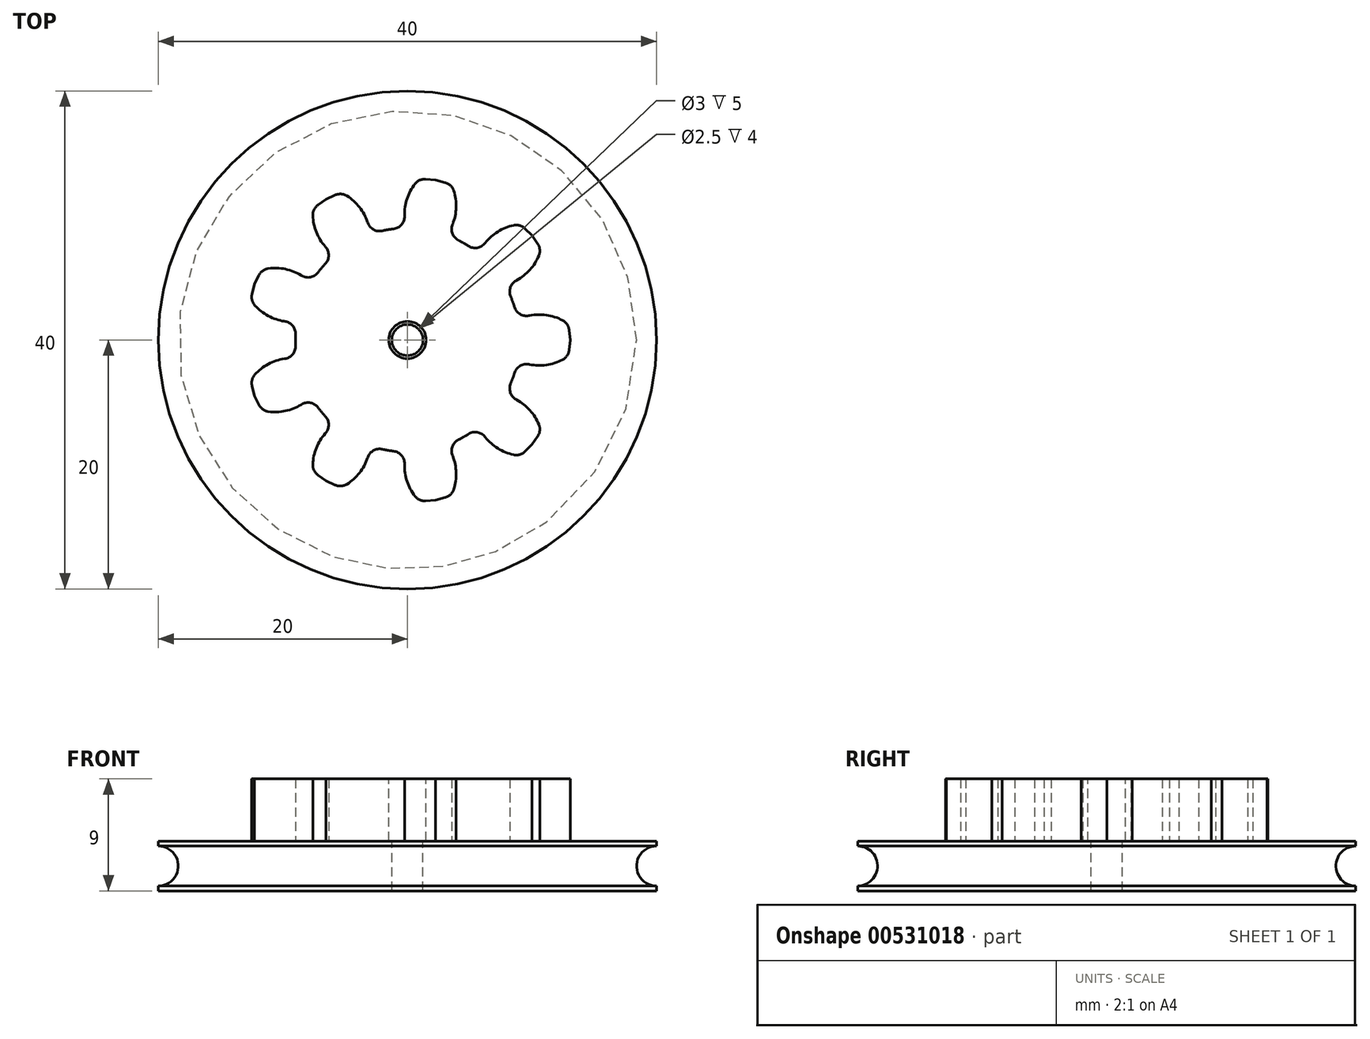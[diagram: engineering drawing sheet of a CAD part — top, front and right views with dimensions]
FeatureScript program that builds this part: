
annotation { "Feature Type Name" : "Feature", "Feature Type Description" : "" }
export const myFeature = defineFeature(function(context is Context, id is Id, definition is map)
    precondition{}
    {
        {
            var Q0;
            Q0=qCreatedBy(makeId("Top.planeOp"),FACE);
            var sketch = newSketch(context, id + "F0", { "sketchPlane" : qUnion([Q0])});
            skCircle(sketch, "E0", {"center": v(0, 0) * mm, "radius": 9 * mm, "construction": true});
            skLineSegment(sketch, "E1", {"start": v(0, 0) * mm, "end": v(11.56, 4.83) * mm, "construction": true});
            skLineSegment(sketch, "E2", {"start": v(0, 0) * mm, "end": v(13.01, 0) * mm, "construction": true});
            skLineSegment(sketch, "E3", {"start": v(0, 0) * mm, "end": v(8.3, 3.47) * mm});
            skLineSegment(sketch, "E4", {"start": v(0, 0) * mm, "end": v(9, 0) * mm});
            skLineSegment(sketch, "E5", {"start": v(0, 0) * mm, "end": v(9.8, 1.96) * mm, "construction": true});
            skLineSegment(sketch, "E6", {"start": v(0, 0) * mm, "end": v(12.94, 1.28) * mm, "construction": true});
            skArc(sketch, "E7", {"start": v(8.3, 3.47) * mm, "mid": v(8.46, 3.06) * mm, "end": v(8.6, 2.64) * mm});
            skLineSegment(sketch, "E8", {"start": v(9.76, 1.96) * mm, "end": v(9.8, 1.96) * mm});
            skLineSegment(sketch, "E9", {"start": v(12.98, 0.8) * mm, "end": v(13.06, 0) * mm});
            skLineSegment(sketch, "E10.MirrorCS", {"start": v(0, 0) * mm, "end": v(8.3, -3.47) * mm});
            skArc(sketch, "E11.MirrorCS", {"start": v(8.3, -3.47) * mm, "mid": v(8.46, -3.06) * mm, "end": v(8.6, -2.64) * mm});
            skLineSegment(sketch, "E12.MirrorCS", {"start": v(9.76, -1.96) * mm, "end": v(9.8, -1.96) * mm});
            skLineSegment(sketch, "E13.MirrorCS", {"start": v(12.98, -0.8) * mm, "end": v(13.06, 0) * mm});
            skPoint(sketch, "E14.visualSharp", {"position": v(8.82, 1.77) * mm});
            skArc(sketch, "E14.filletArc", {"start": v(8.6, 2.64) * mm, "mid": v(9.05, 2.08) * mm, "end": v(9.76, 1.96) * mm});
            skPoint(sketch, "E15.visualSharp", {"position": v(8.82, -1.77) * mm});
            skArc(sketch, "E15.filletArc", {"start": v(9.76, -1.96) * mm, "mid": v(9.05, -2.08) * mm, "end": v(8.6, -2.64) * mm});
            skPoint(sketch, "E16.visualSharp", {"position": v(12.94, -1.28) * mm});
            skArc(sketch, "E16.filletArc", {"start": v(12.46, -1.58) * mm, "mid": v(12.82, -1.26) * mm, "end": v(12.98, -0.8) * mm});
            skPoint(sketch, "E17.visualSharp", {"position": v(12.94, 1.28) * mm});
            skArc(sketch, "E17.filletArc", {"start": v(12.98, 0.8) * mm, "mid": v(12.82, 1.26) * mm, "end": v(12.46, 1.58) * mm});
            skArc(sketch, "E18", {"start": v(12.46, 1.58) * mm, "mid": v(11.16, 2) * mm, "end": v(9.8, 1.96) * mm});
            skArc(sketch, "E19", {"start": v(9.8, -1.96) * mm, "mid": v(11.16, -2) * mm, "end": v(12.46, -1.58) * mm});
            skSolve(sketch);
        }
        {
            var Q0;
            Q0=makeQuery(id+"F0.imprint","IMPRINT",FACE,{"disambiguationData":[TD([[makeQuery(id+"F0.imprint","IMPRINT",EDGE,{"derivedFrom":sQuery(id+"F0.wireOp",EDGE,"E3")}),-1.0]])]});
            extrude(context, id + "F1", {"entities" : qUnion([Q0]), "depth" : 5 * mm, "offsetDistance" : 25 * mm});
        }
        {
            var Q0;
            Q0=makeQuery(id+"F1.opExtrude","SWEPT_BODY",BODY,{"disambiguationData":[OSD([sQuery(id+"F0.wireOp",EDGE,"E3"),sQuery(id+"F0.wireOp",EDGE,"E7"),sQuery(id+"F0.wireOp",EDGE,"E8"),sQuery(id+"F0.wireOp",EDGE,"2mDmJFzi-9lNi-O13z-yd6C-LpkLtRZ1Arxh"),sQuery(id+"F0.wireOp",EDGE,"E9"),sQuery(id+"F0.wireOp",EDGE,"E10.MirrorCS"),sQuery(id+"F0.wireOp",EDGE,"E11.MirrorCS"),sQuery(id+"F0.wireOp",EDGE,"E12.MirrorCS"),sQuery(id+"F0.wireOp",EDGE,"b2a42f57-c3ba-47de-accf-343e7495cc910.MirrorCS"),sQuery(id+"F0.wireOp",EDGE,"E13.MirrorCS"),sQuery(id+"F0.wireOp",EDGE,"E14.filletArc"),sQuery(id+"F0.wireOp",EDGE,"E15.filletArc"),sQuery(id+"F0.wireOp",EDGE,"E16.filletArc"),sQuery(id+"F0.wireOp",EDGE,"E17.filletArc")])]});
            var Q1;
            Q1=makeQuery(id+"F1.opExtrude","SWEPT_EDGE",EDGE,{"disambiguationData":[OSD([sQuery(id+"F0.wireOp",EDGE,"E3"),sQuery(id+"F0.wireOp",EDGE,"E10.MirrorCS")])]});
            circularPattern(context, id + "F2", {"entities" : qUnion([Q0]), "axis" : qUnion([Q1]), "angle" : 360 * degree, "instanceCount" : 9, "equalSpace" : true, "computeTransformsWithoutBuiltin" : true});
        }
        {
            var Q0;
            Q0=makeQuery(id+"F2.opPattern","COPY",BODY,{"derivedFrom":makeQuery(id+"F1.opExtrude","SWEPT_BODY",BODY,{"disambiguationData":[OSD([sQuery(id+"F0.wireOp",EDGE,"E3"),sQuery(id+"F0.wireOp",EDGE,"E7"),sQuery(id+"F0.wireOp",EDGE,"E8"),sQuery(id+"F0.wireOp",EDGE,"2mDmJFzi-9lNi-O13z-yd6C-LpkLtRZ1Arxh"),sQuery(id+"F0.wireOp",EDGE,"E9"),sQuery(id+"F0.wireOp",EDGE,"E10.MirrorCS"),sQuery(id+"F0.wireOp",EDGE,"E11.MirrorCS"),sQuery(id+"F0.wireOp",EDGE,"E12.MirrorCS"),sQuery(id+"F0.wireOp",EDGE,"b2a42f57-c3ba-47de-accf-343e7495cc910.MirrorCS"),sQuery(id+"F0.wireOp",EDGE,"E13.MirrorCS"),sQuery(id+"F0.wireOp",EDGE,"E14.filletArc"),sQuery(id+"F0.wireOp",EDGE,"E15.filletArc"),sQuery(id+"F0.wireOp",EDGE,"E16.filletArc"),sQuery(id+"F0.wireOp",EDGE,"E17.filletArc")])]}),"instanceName":"7"});
            var Q1;
            Q1=makeQuery(id+"F2.opPattern","COPY",BODY,{"derivedFrom":makeQuery(id+"F1.opExtrude","SWEPT_BODY",BODY,{"disambiguationData":[OSD([sQuery(id+"F0.wireOp",EDGE,"E3"),sQuery(id+"F0.wireOp",EDGE,"E7"),sQuery(id+"F0.wireOp",EDGE,"E8"),sQuery(id+"F0.wireOp",EDGE,"2mDmJFzi-9lNi-O13z-yd6C-LpkLtRZ1Arxh"),sQuery(id+"F0.wireOp",EDGE,"E9"),sQuery(id+"F0.wireOp",EDGE,"E10.MirrorCS"),sQuery(id+"F0.wireOp",EDGE,"E11.MirrorCS"),sQuery(id+"F0.wireOp",EDGE,"E12.MirrorCS"),sQuery(id+"F0.wireOp",EDGE,"b2a42f57-c3ba-47de-accf-343e7495cc910.MirrorCS"),sQuery(id+"F0.wireOp",EDGE,"E13.MirrorCS"),sQuery(id+"F0.wireOp",EDGE,"E14.filletArc"),sQuery(id+"F0.wireOp",EDGE,"E15.filletArc"),sQuery(id+"F0.wireOp",EDGE,"E16.filletArc"),sQuery(id+"F0.wireOp",EDGE,"E17.filletArc")])]}),"instanceName":"6"});
            var Q2;
            Q2=makeQuery(id+"F2.opPattern","COPY",BODY,{"derivedFrom":makeQuery(id+"F1.opExtrude","SWEPT_BODY",BODY,{"disambiguationData":[OSD([sQuery(id+"F0.wireOp",EDGE,"E3"),sQuery(id+"F0.wireOp",EDGE,"E7"),sQuery(id+"F0.wireOp",EDGE,"E8"),sQuery(id+"F0.wireOp",EDGE,"2mDmJFzi-9lNi-O13z-yd6C-LpkLtRZ1Arxh"),sQuery(id+"F0.wireOp",EDGE,"E9"),sQuery(id+"F0.wireOp",EDGE,"E10.MirrorCS"),sQuery(id+"F0.wireOp",EDGE,"E11.MirrorCS"),sQuery(id+"F0.wireOp",EDGE,"E12.MirrorCS"),sQuery(id+"F0.wireOp",EDGE,"b2a42f57-c3ba-47de-accf-343e7495cc910.MirrorCS"),sQuery(id+"F0.wireOp",EDGE,"E13.MirrorCS"),sQuery(id+"F0.wireOp",EDGE,"E14.filletArc"),sQuery(id+"F0.wireOp",EDGE,"E15.filletArc"),sQuery(id+"F0.wireOp",EDGE,"E16.filletArc"),sQuery(id+"F0.wireOp",EDGE,"E17.filletArc")])]}),"instanceName":"4"});
            var Q3;
            Q3=makeQuery(id+"F2.opPattern","COPY",BODY,{"derivedFrom":makeQuery(id+"F1.opExtrude","SWEPT_BODY",BODY,{"disambiguationData":[OSD([sQuery(id+"F0.wireOp",EDGE,"E3"),sQuery(id+"F0.wireOp",EDGE,"E7"),sQuery(id+"F0.wireOp",EDGE,"E8"),sQuery(id+"F0.wireOp",EDGE,"2mDmJFzi-9lNi-O13z-yd6C-LpkLtRZ1Arxh"),sQuery(id+"F0.wireOp",EDGE,"E9"),sQuery(id+"F0.wireOp",EDGE,"E10.MirrorCS"),sQuery(id+"F0.wireOp",EDGE,"E11.MirrorCS"),sQuery(id+"F0.wireOp",EDGE,"E12.MirrorCS"),sQuery(id+"F0.wireOp",EDGE,"b2a42f57-c3ba-47de-accf-343e7495cc910.MirrorCS"),sQuery(id+"F0.wireOp",EDGE,"E13.MirrorCS"),sQuery(id+"F0.wireOp",EDGE,"E14.filletArc"),sQuery(id+"F0.wireOp",EDGE,"E15.filletArc"),sQuery(id+"F0.wireOp",EDGE,"E16.filletArc"),sQuery(id+"F0.wireOp",EDGE,"E17.filletArc")])]}),"instanceName":"5"});
            var Q4;
            Q4=makeQuery(id+"F1.opExtrude","SWEPT_BODY",BODY,{"disambiguationData":[OSD([sQuery(id+"F0.wireOp",EDGE,"E3"),sQuery(id+"F0.wireOp",EDGE,"E7"),sQuery(id+"F0.wireOp",EDGE,"E8"),sQuery(id+"F0.wireOp",EDGE,"2mDmJFzi-9lNi-O13z-yd6C-LpkLtRZ1Arxh"),sQuery(id+"F0.wireOp",EDGE,"E9"),sQuery(id+"F0.wireOp",EDGE,"E10.MirrorCS"),sQuery(id+"F0.wireOp",EDGE,"E11.MirrorCS"),sQuery(id+"F0.wireOp",EDGE,"E12.MirrorCS"),sQuery(id+"F0.wireOp",EDGE,"b2a42f57-c3ba-47de-accf-343e7495cc910.MirrorCS"),sQuery(id+"F0.wireOp",EDGE,"E13.MirrorCS"),sQuery(id+"F0.wireOp",EDGE,"E14.filletArc"),sQuery(id+"F0.wireOp",EDGE,"E15.filletArc"),sQuery(id+"F0.wireOp",EDGE,"E16.filletArc"),sQuery(id+"F0.wireOp",EDGE,"E17.filletArc")])]});
            var Q5;
            Q5=makeQuery(id+"F2.opPattern","COPY",BODY,{"derivedFrom":makeQuery(id+"F1.opExtrude","SWEPT_BODY",BODY,{"disambiguationData":[OSD([sQuery(id+"F0.wireOp",EDGE,"E3"),sQuery(id+"F0.wireOp",EDGE,"E7"),sQuery(id+"F0.wireOp",EDGE,"E8"),sQuery(id+"F0.wireOp",EDGE,"2mDmJFzi-9lNi-O13z-yd6C-LpkLtRZ1Arxh"),sQuery(id+"F0.wireOp",EDGE,"E9"),sQuery(id+"F0.wireOp",EDGE,"E10.MirrorCS"),sQuery(id+"F0.wireOp",EDGE,"E11.MirrorCS"),sQuery(id+"F0.wireOp",EDGE,"E12.MirrorCS"),sQuery(id+"F0.wireOp",EDGE,"b2a42f57-c3ba-47de-accf-343e7495cc910.MirrorCS"),sQuery(id+"F0.wireOp",EDGE,"E13.MirrorCS"),sQuery(id+"F0.wireOp",EDGE,"E14.filletArc"),sQuery(id+"F0.wireOp",EDGE,"E15.filletArc"),sQuery(id+"F0.wireOp",EDGE,"E16.filletArc"),sQuery(id+"F0.wireOp",EDGE,"E17.filletArc")])]}),"instanceName":"1"});
            var Q6;
            Q6=makeQuery(id+"F2.opPattern","COPY",BODY,{"derivedFrom":makeQuery(id+"F1.opExtrude","SWEPT_BODY",BODY,{"disambiguationData":[OSD([sQuery(id+"F0.wireOp",EDGE,"E3"),sQuery(id+"F0.wireOp",EDGE,"E7"),sQuery(id+"F0.wireOp",EDGE,"E8"),sQuery(id+"F0.wireOp",EDGE,"2mDmJFzi-9lNi-O13z-yd6C-LpkLtRZ1Arxh"),sQuery(id+"F0.wireOp",EDGE,"E9"),sQuery(id+"F0.wireOp",EDGE,"E10.MirrorCS"),sQuery(id+"F0.wireOp",EDGE,"E11.MirrorCS"),sQuery(id+"F0.wireOp",EDGE,"E12.MirrorCS"),sQuery(id+"F0.wireOp",EDGE,"b2a42f57-c3ba-47de-accf-343e7495cc910.MirrorCS"),sQuery(id+"F0.wireOp",EDGE,"E13.MirrorCS"),sQuery(id+"F0.wireOp",EDGE,"E14.filletArc"),sQuery(id+"F0.wireOp",EDGE,"E15.filletArc"),sQuery(id+"F0.wireOp",EDGE,"E16.filletArc"),sQuery(id+"F0.wireOp",EDGE,"E17.filletArc")])]}),"instanceName":"3"});
            var Q7;
            Q7=makeQuery(id+"F2.opPattern","COPY",BODY,{"derivedFrom":makeQuery(id+"F1.opExtrude","SWEPT_BODY",BODY,{"disambiguationData":[OSD([sQuery(id+"F0.wireOp",EDGE,"E3"),sQuery(id+"F0.wireOp",EDGE,"E7"),sQuery(id+"F0.wireOp",EDGE,"E8"),sQuery(id+"F0.wireOp",EDGE,"2mDmJFzi-9lNi-O13z-yd6C-LpkLtRZ1Arxh"),sQuery(id+"F0.wireOp",EDGE,"E9"),sQuery(id+"F0.wireOp",EDGE,"E10.MirrorCS"),sQuery(id+"F0.wireOp",EDGE,"E11.MirrorCS"),sQuery(id+"F0.wireOp",EDGE,"E12.MirrorCS"),sQuery(id+"F0.wireOp",EDGE,"b2a42f57-c3ba-47de-accf-343e7495cc910.MirrorCS"),sQuery(id+"F0.wireOp",EDGE,"E13.MirrorCS"),sQuery(id+"F0.wireOp",EDGE,"E14.filletArc"),sQuery(id+"F0.wireOp",EDGE,"E15.filletArc"),sQuery(id+"F0.wireOp",EDGE,"E16.filletArc"),sQuery(id+"F0.wireOp",EDGE,"E17.filletArc")])]}),"instanceName":"2"});
            var Q8;
            Q8=makeQuery(id+"F2.opPattern","COPY",BODY,{"derivedFrom":makeQuery(id+"F1.opExtrude","SWEPT_BODY",BODY,{"disambiguationData":[OSD([sQuery(id+"F0.wireOp",EDGE,"E3"),sQuery(id+"F0.wireOp",EDGE,"E7"),sQuery(id+"F0.wireOp",EDGE,"E8"),sQuery(id+"F0.wireOp",EDGE,"E9"),sQuery(id+"F0.wireOp",EDGE,"E10.MirrorCS"),sQuery(id+"F0.wireOp",EDGE,"E11.MirrorCS"),sQuery(id+"F0.wireOp",EDGE,"E12.MirrorCS"),sQuery(id+"F0.wireOp",EDGE,"E13.MirrorCS"),sQuery(id+"F0.wireOp",EDGE,"E14.filletArc"),sQuery(id+"F0.wireOp",EDGE,"E15.filletArc"),sQuery(id+"F0.wireOp",EDGE,"E16.filletArc"),sQuery(id+"F0.wireOp",EDGE,"E17.filletArc"),sQuery(id+"F0.wireOp",EDGE,"E18"),sQuery(id+"F0.wireOp",EDGE,"E19")])]}),"instanceName":"8"});
            booleanBodies(context, id + "F3", {"operationType" : BooleanOperationType.UNION, "tools" : qUnion([Q0, Q1, Q2, Q3, Q4, Q5, Q6, Q7, Q8])});
        }
        {
            var Q0;
            {var subQ0=makeQuery(id+"F1.opExtrude","CAP_FACE",FACE,{"disambiguationData":[OSD([sQuery(id+"F0.wireOp",EDGE,"E3"),sQuery(id+"F0.wireOp",EDGE,"E7"),sQuery(id+"F0.wireOp",EDGE,"E8"),sQuery(id+"F0.wireOp",EDGE,"E9"),sQuery(id+"F0.wireOp",EDGE,"E10.MirrorCS"),sQuery(id+"F0.wireOp",EDGE,"E11.MirrorCS"),sQuery(id+"F0.wireOp",EDGE,"E12.MirrorCS"),sQuery(id+"F0.wireOp",EDGE,"E13.MirrorCS"),sQuery(id+"F0.wireOp",EDGE,"E14.filletArc"),sQuery(id+"F0.wireOp",EDGE,"E15.filletArc"),sQuery(id+"F0.wireOp",EDGE,"E16.filletArc"),sQuery(id+"F0.wireOp",EDGE,"E17.filletArc"),sQuery(id+"F0.wireOp",EDGE,"E18"),sQuery(id+"F0.wireOp",EDGE,"E19")])],"isStart":false});Q0=makeQuery(id+"F3.opBoolean","MERGE",FACE,{"derivedFrom":[subQ0,makeQuery(id+"F2.opPattern","COPY",FACE,{"derivedFrom":subQ0,"instanceName":"1"}),makeQuery(id+"F2.opPattern","COPY",FACE,{"derivedFrom":subQ0,"instanceName":"2"}),makeQuery(id+"F2.opPattern","COPY",FACE,{"derivedFrom":subQ0,"instanceName":"3"}),makeQuery(id+"F2.opPattern","COPY",FACE,{"derivedFrom":subQ0,"instanceName":"4"}),makeQuery(id+"F2.opPattern","COPY",FACE,{"derivedFrom":subQ0,"instanceName":"5"}),makeQuery(id+"F2.opPattern","COPY",FACE,{"derivedFrom":subQ0,"instanceName":"6"}),makeQuery(id+"F2.opPattern","COPY",FACE,{"derivedFrom":subQ0,"instanceName":"7"}),makeQuery(id+"F2.opPattern","COPY",FACE,{"derivedFrom":subQ0,"instanceName":"8"})]});}
            var sketch = newSketch(context, id + "F4", { "sketchPlane" : qUnion([Q0])});
            skCircle(sketch, "E20", {"center": v(0, 0) * mm, "radius": 1.5 * mm});
            skSolve(sketch);
        }
        {
            var Q0;
            Q0=qSketchRegion(id+"F4",true);
            var Q1;
            {var subQ0=makeQuery(id+"F1.opExtrude","CAP_FACE",FACE,{"disambiguationData":[OSD([sQuery(id+"F0.wireOp",EDGE,"E3"),sQuery(id+"F0.wireOp",EDGE,"E7"),sQuery(id+"F0.wireOp",EDGE,"E8"),sQuery(id+"F0.wireOp",EDGE,"E9"),sQuery(id+"F0.wireOp",EDGE,"E10.MirrorCS"),sQuery(id+"F0.wireOp",EDGE,"E11.MirrorCS"),sQuery(id+"F0.wireOp",EDGE,"E12.MirrorCS"),sQuery(id+"F0.wireOp",EDGE,"E13.MirrorCS"),sQuery(id+"F0.wireOp",EDGE,"E14.filletArc"),sQuery(id+"F0.wireOp",EDGE,"E15.filletArc"),sQuery(id+"F0.wireOp",EDGE,"E16.filletArc"),sQuery(id+"F0.wireOp",EDGE,"E17.filletArc"),sQuery(id+"F0.wireOp",EDGE,"E18"),sQuery(id+"F0.wireOp",EDGE,"E19")])],"isStart":true});Q1=makeQuery(id+"F3.opBoolean","MERGE",FACE,{"derivedFrom":[subQ0,makeQuery(id+"F2.opPattern","COPY",FACE,{"derivedFrom":subQ0,"instanceName":"1"}),makeQuery(id+"F2.opPattern","COPY",FACE,{"derivedFrom":subQ0,"instanceName":"2"}),makeQuery(id+"F2.opPattern","COPY",FACE,{"derivedFrom":subQ0,"instanceName":"3"}),makeQuery(id+"F2.opPattern","COPY",FACE,{"derivedFrom":subQ0,"instanceName":"4"}),makeQuery(id+"F2.opPattern","COPY",FACE,{"derivedFrom":subQ0,"instanceName":"5"}),makeQuery(id+"F2.opPattern","COPY",FACE,{"derivedFrom":subQ0,"instanceName":"6"}),makeQuery(id+"F2.opPattern","COPY",FACE,{"derivedFrom":subQ0,"instanceName":"7"}),makeQuery(id+"F2.opPattern","COPY",FACE,{"derivedFrom":subQ0,"instanceName":"8"})]});}
            extrude(context, id + "F5", {"entities" : qUnion([Q0]), "operationType" : NewBodyOperationType.REMOVE, "endBound" : BoundingType.UP_TO_SURFACE, "oppositeDirection" : true, "depth" : 25 * mm, "endBoundEntityFace" : qUnion([Q1]), "offsetDistance" : 25 * mm});
        }
        {
            var Q0;
            Q0=qCreatedBy(makeId("Right.planeOp"),FACE);
            var sketch = newSketch(context, id + "F6", { "sketchPlane" : qUnion([Q0])});
            skLineSegment(sketch, "E21", {"start": v(0, 0) * mm, "end": v(1.25, 0) * mm, "construction": true});
            skLineSegment(sketch, "E22", {"start": v(0, 0) * mm, "end": v(0, -3.03) * mm, "construction": true});
            skLineSegment(sketch, "E23", {"start": v(1.25, 0) * mm, "end": v(20, 0) * mm});
            skLineSegment(sketch, "E24", {"start": v(20, 0) * mm, "end": v(20, -0.4) * mm});
            skLineSegment(sketch, "E25", {"start": v(20, -0.4) * mm, "end": v(20, -2) * mm, "construction": true});
            skLineSegment(sketch, "E26", {"start": v(20, -2) * mm, "end": v(20, -3.6) * mm, "construction": true});
            skLineSegment(sketch, "E27", {"start": v(20, -3.6) * mm, "end": v(20, -4) * mm});
            skLineSegment(sketch, "E28", {"start": v(20, -4) * mm, "end": v(1.25, -4) * mm});
            skLineSegment(sketch, "E29", {"start": v(20, -2) * mm, "end": v(18.4, -2) * mm, "construction": true});
            skArc(sketch, "E30", {"start": v(20, -0.4) * mm, "mid": v(18.4, -2) * mm, "end": v(20, -3.6) * mm});
            skLineSegment(sketch, "E31", {"start": v(1.25, -4) * mm, "end": v(1.25, 0) * mm});
            skPoint(sketch, "E32.center", {"position": v(0, 0) * mm});
            skSolve(sketch);
        }
        {
            var Q0;
            Q0=makeQuery(id+"F6.imprint","IMPRINT",FACE,{"disambiguationData":[TD([[makeQuery(id+"F6.imprint","IMPRINT",EDGE,{"derivedFrom":sQuery(id+"F6.wireOp",EDGE,"E23")}),-1.0]])]});
            var Q1;
            Q1=sQuery(id+"F6.wireOp",EDGE,"E22");
            revolve(context, id + "F7", {"operationType" : NewBodyOperationType.ADD, "entities" : qUnion([Q0]), "axis" : qUnion([Q1]), "revolveType" : RevolveType.FULL});
        }
    });
